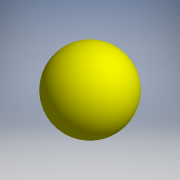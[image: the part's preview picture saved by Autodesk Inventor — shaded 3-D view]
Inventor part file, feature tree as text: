
AUTODESK INVENTOR PART (.ipt)
format: ipt  version: 2017.3 (Build 213256000, 256)  size: 117,760 bytes
history: native  units: mm (DEFAULTED — no unit token found)
features: revolve x1, sketch x1
ambient origin geometry x8: Origin, YZ Plane, XZ Plane, XY Plane, X Axis, Y Axis, Z Axis, Center Point
bodies: Solid1 (feature_tree)
feature tree (2):
  revolve  "Revolution1"  [1 undecoded]
  sketch  "Sketch_6"  dims[d0=360.0deg]
note: 1 required parameter value undecoded (feature->parameter linkage not recoverable at this tier; creation-order binding heuristic only, values carry confidence <= 0.55)
